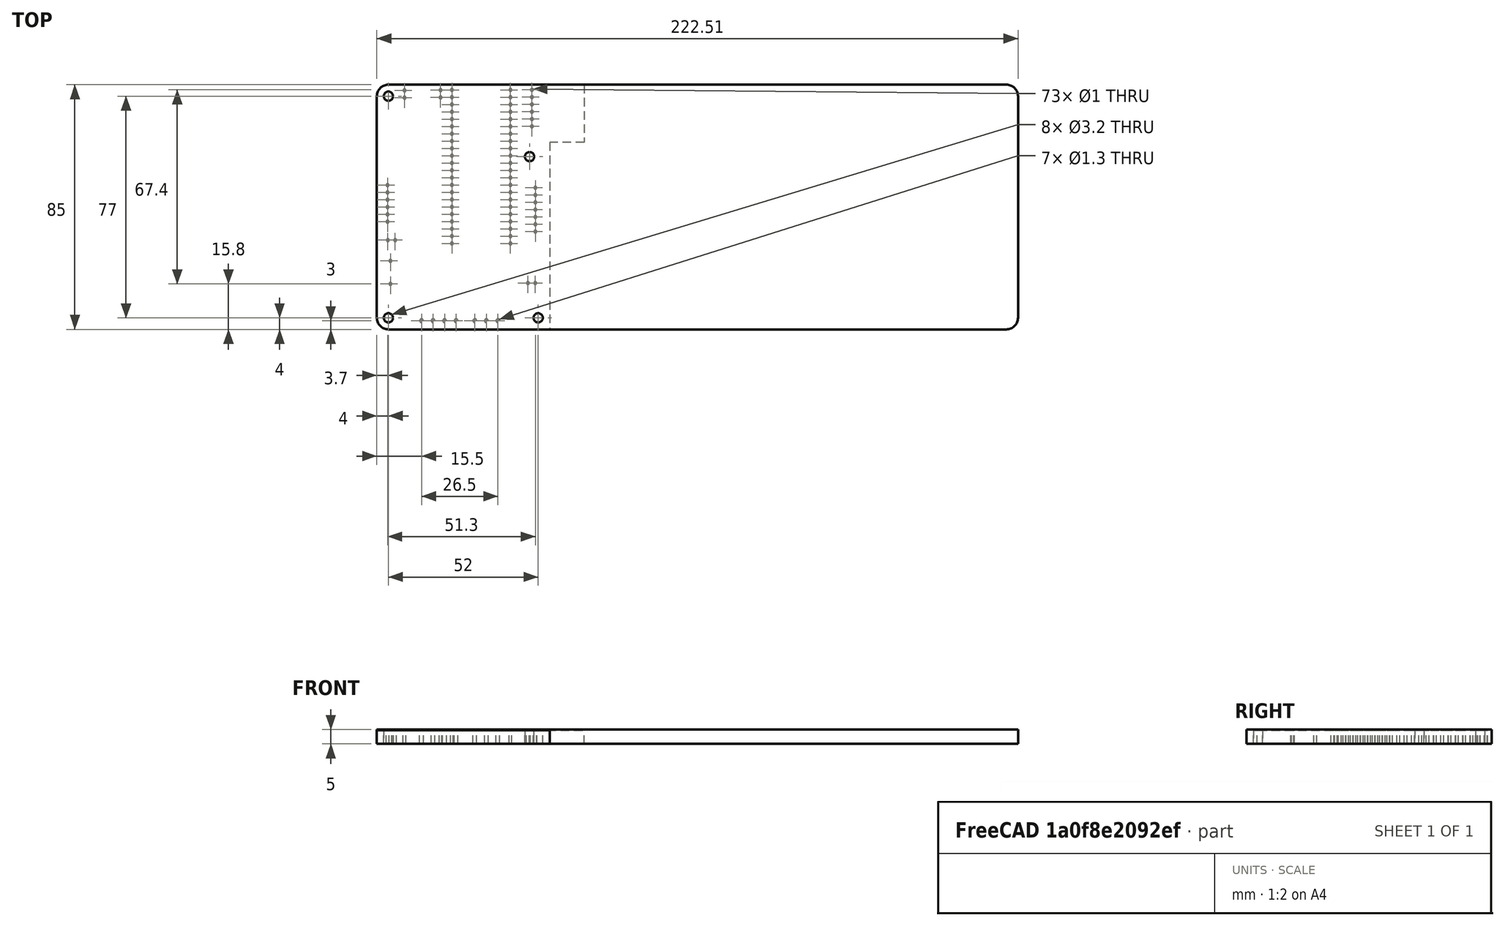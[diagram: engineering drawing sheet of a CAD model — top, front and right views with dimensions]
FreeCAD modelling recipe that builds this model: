
FCSTD DOCUMENT  (FreeCAD 0.18.4R)
Label: GbSwitchFp_bas
License: All rights reserved
LicenseURL: http://en.wikipedia.org/wiki/All_rights_reserved
objects: Part::Feature×1, Sketcher::SketchObject×1, Part::Extrusion×1
note: 3 computed .brp shape members not serialized (recipe doc carries the construction recipe); baked Part::Feature solids carry a one-line shape summary decoded from their .brp

FEATURE [Part::Feature] Solid  label="GbSwitchFp 1"
  shape: bbox 72 x 85 x 4.69 mm, 94 faces (baked)
FEATURE [Sketcher::SketchObject] Sketch
  ExternalGeometry = -> [Solid]
  MapMode = 2
  Support = -> [Solid]
  sketch-geometry (13):
    g0: Circle CenterX=4 CenterY=-4 CenterZ=0 NormalX=0 NormalY=0 NormalZ=1 AngleXU=0 Radius=1.6
    g1: Circle CenterX=53 CenterY=-25 CenterZ=0 NormalX=0 NormalY=0 NormalZ=1 AngleXU=0 Radius=1.6
    g2: Circle CenterX=4 CenterY=-81 CenterZ=0 NormalX=0 NormalY=0 NormalZ=1 AngleXU=0 Radius=1.6
    g3: Circle CenterX=56 CenterY=-81 CenterZ=0 NormalX=0 NormalY=0 NormalZ=1 AngleXU=0 Radius=1.6
    g4: LineSegment StartX=0 StartY=-4 StartZ=0 EndX=0 EndY=-81 EndZ=0
    g5: LineSegment StartX=4 StartY=-85 StartZ=0 EndX=218.511 EndY=-85 EndZ=0
    g6: LineSegment StartX=4 StartY=0 StartZ=0 EndX=72 EndY=0 EndZ=0
    g7: ArcOfCircle CenterX=4 CenterY=-4 CenterZ=0 NormalX=0 NormalY=0 NormalZ=1 AngleXU=0 Radius=4 StartAngle=1.5708 EndAngle=3.14159
    g8: ArcOfCircle CenterX=4 CenterY=-81 CenterZ=0 NormalX=0 NormalY=0 NormalZ=1 AngleXU=0 Radius=4 StartAngle=3.14159 EndAngle=4.71239
    g9: LineSegment StartX=72 StartY=0 StartZ=0 EndX=218.511 EndY=2.577e-13 EndZ=0
    g10: LineSegment StartX=222.511 StartY=-4 StartZ=0 EndX=222.511 EndY=-81 EndZ=0
    g11: ArcOfCircle CenterX=218.511 CenterY=-81 CenterZ=0 NormalX=0 NormalY=0 NormalZ=1 AngleXU=0 Radius=4 StartAngle=4.71239 EndAngle=6.28319
    g12: ArcOfCircle CenterX=218.511 CenterY=-4 CenterZ=0 NormalX=0 NormalY=0 NormalZ=1 AngleXU=0 Radius=4 StartAngle=0 EndAngle=1.5708
  constraints (25):
    c: Coincident(g0,g-9)
    c: Coincident(g1,g-10)
    c: Coincident(g2,g-11)
    c: Coincident(g3,g-12)
    c: Coincident(g4,g-7)
    c: Coincident(g4,g-6)
    c: Coincident(g5,g-5)
    c: Coincident(g6,g-8)
    c: Coincident(g6,g-8)
    c: Coincident(g7,g6)
    c: Coincident(g7,g4)
    c: Coincident(g5,g8)
    c: Coincident(g8,g4)
    c: Coincident(g9,g6)
    c: Tangent(g5,g11) = -1.5708
    c: Tangent(g10,g11) = 1.5708
    c: Radius(g8) = 4
    c: Radius(g7) = 4
    c: Radius(g11) = 4
    c: Parallel(g5,g6)
    c: Parallel(g10,g4)
    c: Tangent(g9,g12) = 1.5708
    c: Tangent(g10,g12) = 1.5708
    c: Radius(g12) = 4
    c: Parallel(g9,g5)
FEATURE [Part::Extrusion] Extrude
  Base = -> Sketch
  Dir = (0,0,1)
  DirMode = 2
  FaceMakerClass = Part::FaceMakerBullseye
  LengthFwd = 5
  LengthRev = 0
  Solid = true
  Symmetric = false
